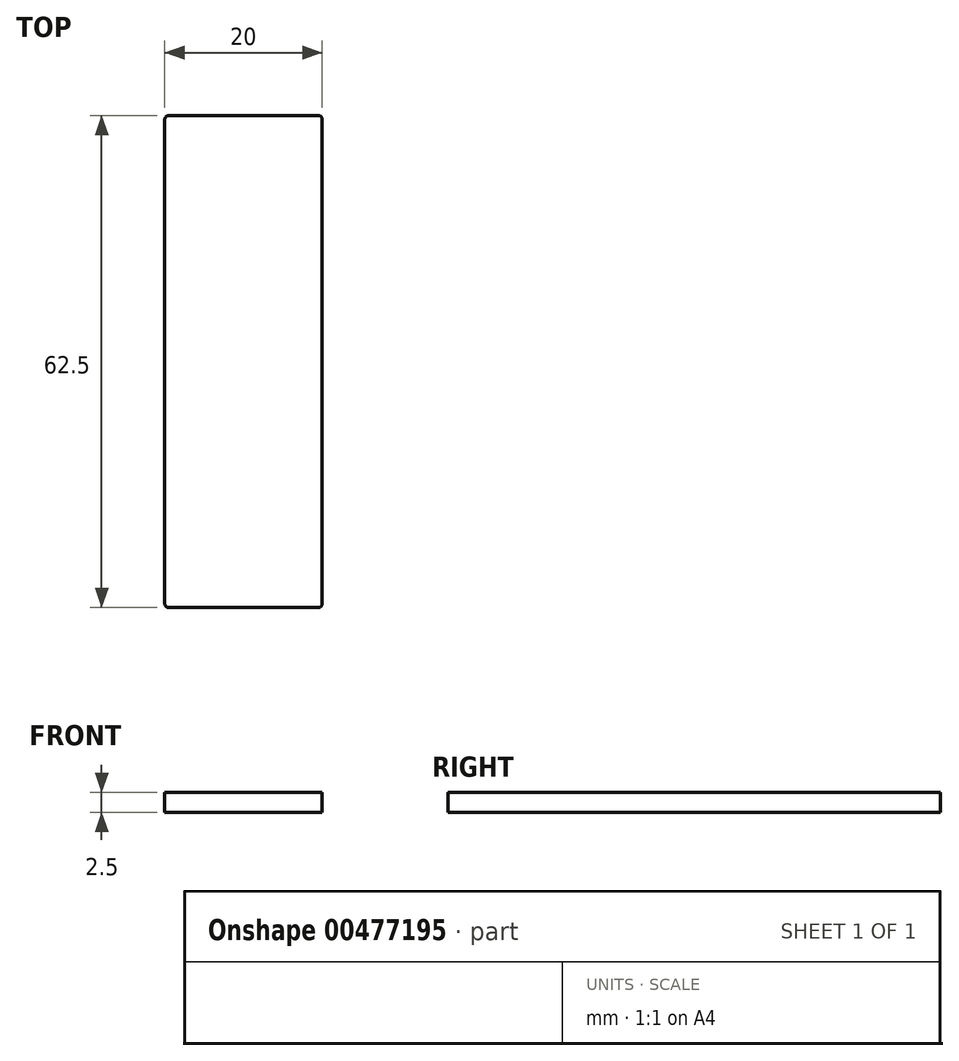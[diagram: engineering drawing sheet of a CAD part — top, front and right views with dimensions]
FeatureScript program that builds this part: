
annotation { "Feature Type Name" : "Feature", "Feature Type Description" : "" }
export const myFeature = defineFeature(function(context is Context, id is Id, definition is map)
    precondition{}
    {
        {
            var Q0;
            Q0=qCreatedBy(makeId("Top.planeOp"),FACE);
            var sketch = newSketch(context, id + "F0", { "sketchPlane" : qUnion([Q0])});
            skLineSegment(sketch, "E0.bottom", {"start": v(-20, 62.5) * mm, "end": v(20, 62.5) * mm});
            skLineSegment(sketch, "E0.top", {"start": v(-20, -62.5) * mm, "end": v(20, -62.5) * mm});
            skLineSegment(sketch, "E0.left", {"start": v(-20, 62.5) * mm, "end": v(-20, -62.5) * mm});
            skLineSegment(sketch, "E0.right", {"start": v(20, 62.5) * mm, "end": v(20, -62.5) * mm});
            skPoint(sketch, "E0.middle", {"position": v(0, 0) * mm});
            skSolve(sketch);
        }
        {
            var Q0;
            Q0=qSketchRegion(id+"F0",true);
            extrude(context, id + "F1", {"entities" : qUnion([Q0]), "oppositeDirection" : true, "depth" : 5 * mm});
        }
        {
            var Q0;
            Q0=makeQuery(id+"F1.opExtrude","SWEPT_EDGE",EDGE,{"disambiguationData":[OSD([sQuery(id+"F0.wireOp",EDGE,"E0.top"),sQuery(id+"F0.wireOp",EDGE,"E0.left")])]});
            var Q1;
            Q1=makeQuery(id+"F1.opExtrude","SWEPT_EDGE",EDGE,{"disambiguationData":[OSD([sQuery(id+"F0.wireOp",EDGE,"E0.bottom"),sQuery(id+"F0.wireOp",EDGE,"E0.left")])]});
            var Q2;
            Q2=makeQuery(id+"F1.opExtrude","SWEPT_EDGE",EDGE,{"disambiguationData":[OSD([sQuery(id+"F0.wireOp",EDGE,"E0.top"),sQuery(id+"F0.wireOp",EDGE,"E0.right")])]});
            var Q3;
            Q3=makeQuery(id+"F1.opExtrude","SWEPT_EDGE",EDGE,{"disambiguationData":[OSD([sQuery(id+"F0.wireOp",EDGE,"E0.bottom"),sQuery(id+"F0.wireOp",EDGE,"E0.right")])]});
            fillet(context, id + "F2", {"entities" : qUnion([Q0, Q1, Q2, Q3]), "radius" : 1 * mm, "tangentPropagation" : true, "allowEdgeOverflow" : false});
        }
        {
            var Q0;
            Q0=makeQuery(id+"F1.opExtrude","SWEPT_BODY",BODY,{"disambiguationData":[OSD([sQuery(id+"F0.wireOp",EDGE,"E0.bottom"),sQuery(id+"F0.wireOp",EDGE,"E0.top"),sQuery(id+"F0.wireOp",EDGE,"E0.left"),sQuery(id+"F0.wireOp",EDGE,"E0.right")])]});
            var Q1;
            Q1=qCreatedBy(makeId("Origin.pointOp"),VERTEX);
            transform(context, id + "F3", {"entities" : qUnion([Q0]), "transformType" : TransformType.SCALE_UNIFORMLY, "scale" : 0.5, "scalePoint" : qUnion([Q1]), "makeCopy" : false});
        }
    });
